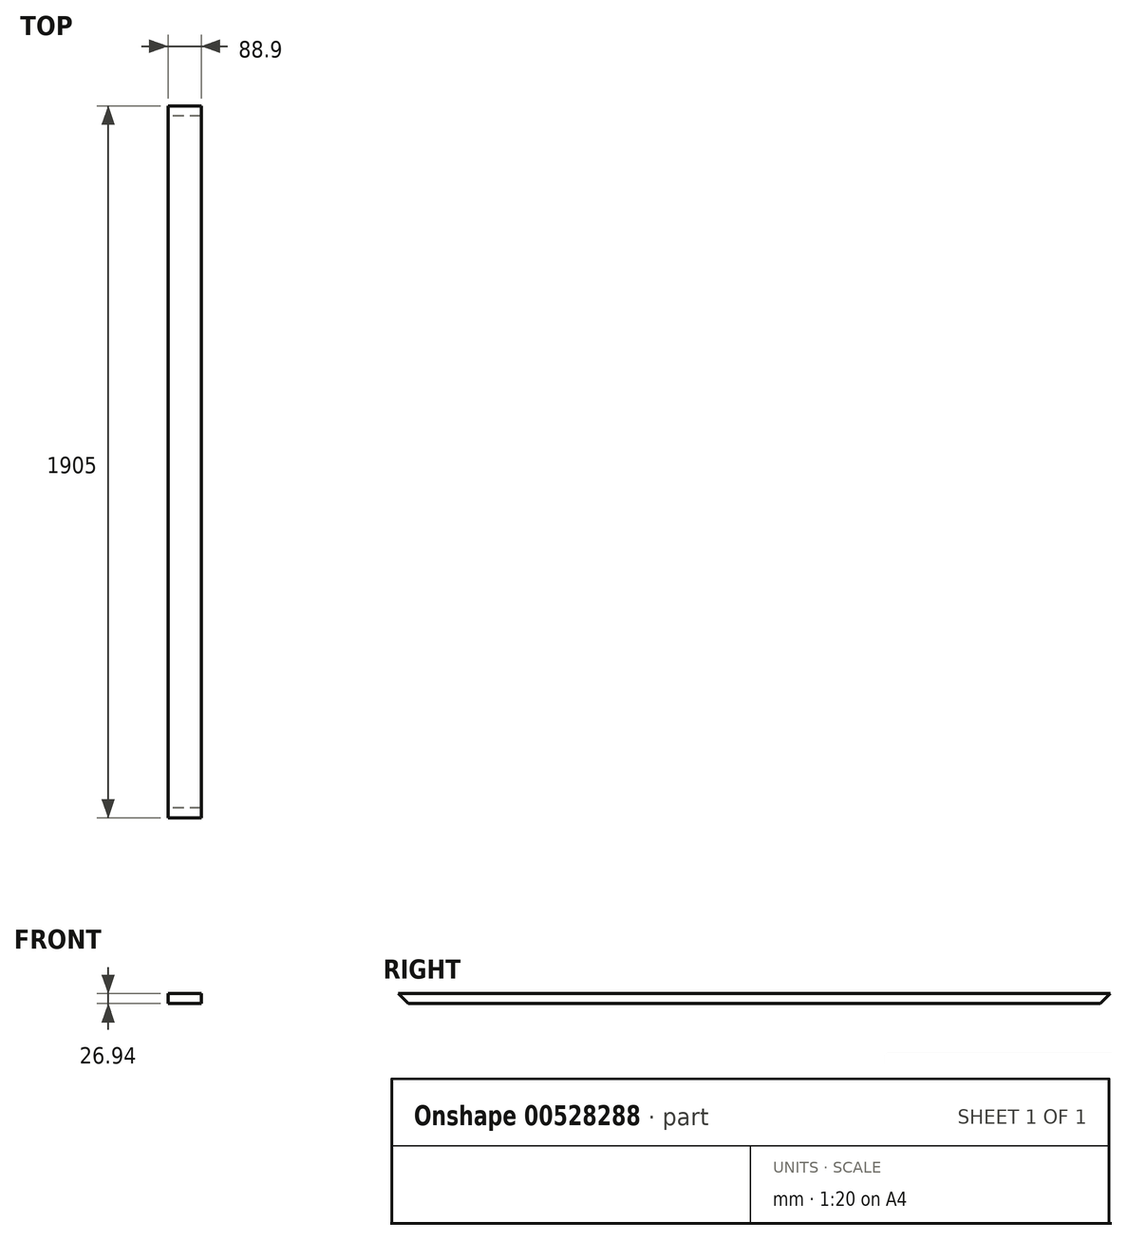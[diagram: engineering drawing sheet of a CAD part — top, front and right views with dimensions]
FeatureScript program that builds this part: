
annotation { "Feature Type Name" : "Feature", "Feature Type Description" : "" }
export const myFeature = defineFeature(function(context is Context, id is Id, definition is map)
    precondition{}
    {
        {
            var Q0;
            Q0=qCreatedBy(makeId("Right.planeOp"),FACE);
            var sketch = newSketch(context, id + "F0", { "sketchPlane" : qUnion([Q0])});
            skLineSegment(sketch, "E0", {"start": v(-1006.36, 26.94) * mm, "end": v(898.64, 26.94) * mm});
            skLineSegment(sketch, "E1", {"start": v(-1006.36, 26.94) * mm, "end": v(-979.42, 0) * mm});
            skLineSegment(sketch, "E2", {"start": v(898.64, 26.94) * mm, "end": v(871.7, 0) * mm});
            skLineSegment(sketch, "E3", {"start": v(871.7, 0) * mm, "end": v(-979.42, 0) * mm});
            skSolve(sketch);
        }
        {
            var Q0;
            Q0 = qSketchRegion(id + "F0", true);
            extrude(context, id + "F1", {"entities" : qUnion([Q0]), "depth" : 88.9 * mm, "offsetDistance" : 25.4 * mm});
        }
    });
